SOLIDWORKS PART (.sldprt)
format: sldprt  version: not decoded by parser v0  size: 129,024 bytes
history: native  units: mm
features: plane x4, sketch x4, material x1, extrude x1, helix x1, sweep x1 (+13 scaffold rows collapsed)
feature tree (25):
  scaffold x13  (default folders/planes/origin — collapsed)
  material  "材质 <未指定>"
  plane  "前视基准面"
  plane  "上视基准面"
  plane  "右视基准面"
  sketch  "草图1"  dims[c1.D1=3.0mm c1.D2=1.0mm c2.D1=~2.592383mm c2.D2=0.2mm c2.D3=0.2mm c3.D1=0.2mm c3.D4=1.5mm]
  extrude  "凸台-拉伸1"  Depth=0.4mm
  sketch  "草图2"  dims[D1=~0.233662mm]
  helix  "螺旋线/涡状线1"  Pitch=1mm
  sketch  "草图3"
  plane  "基准面1"
  sketch  "草图4"  dims[D2=~0.018031mm D1=0.2mm]
  sweep  "扫描1"
decode coverage: 5 of 7 modeling features carry decoded parameters
note: ~ marks probable driven/reference dimensions
note: suppression state not decoded; provenance and decode notes live in map.json
